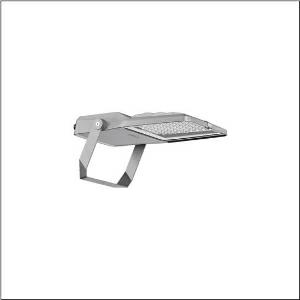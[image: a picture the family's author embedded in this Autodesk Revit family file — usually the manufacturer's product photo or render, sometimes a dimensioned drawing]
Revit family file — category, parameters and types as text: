
# Revit family: floodlight_fl_21_iq_mini___pl33t_5xa7771d4f1a_3e9c
name_source: partatom
category: Lighting Fixtures
units: mm (PartAtom-declared; Revit-internal decimal feet)

## family parameters
Cut with Voids When Loaded = No
Host = Face
Light Source = No
Part Type = Normal
Room Calculation Point = No
Round Connector Dimension = Use Diameter
Shared = No

## types (1)
- --- (1 x LED, 18390 lm, 143 W, 4000K)
    Apparent Load = 143 VA
    CIE Flux Codes = 26 75 99 100 100
    Color Rendering = 70
    Color Temperature = 4000K
    Default Elevation = 1800 mm
    Description = Floodlight FL 21 iQ mini, floodlight, primary light control with lens, of PMMA, primary optical cover: protective disc, of toughened safety glass, transparent, light distribution: PL33T, light emission: direct distribution, installation type: surface-mounted, lamps: LED, High Power LED, rated values: 18.390lm | 143W | 128,6lm/W (begin service life); end service life: 18.390lm | 151,6W; at 50% lumin. flux: 9.195lm | 60,8W | 151,2lm/W, colour temperature: 4000K, colour rendering: CRI > 70, light colour: 740, light setting 1 begin service life: 100% | 18.390lm | 143W | 128,6lm/W | 4.000K, light setting 1 end service life: 151,6W, further light settings possible, control: Auto-Match, Temp-Guard, Lumen-Switch, Night-Set, Smart-Wire, Light-Fading, Desk-Remote (wireless, voltage-free reading and setting of iQ features in the workshop via application-optimized NFC function/RFID function), optimised constant luminous flux control (CLO 2.0), pre-setting: linear dimming characteristic, with terminal, 6-pole, mains connection: 220..240V, AC, 50/60Hz, luminaire housing, of diecast aluminium, powder-coated, SITECO metallic grey (DB 702S), corrosivity category C5 mid according to DIN EN ISO 12944suitable for swimming poolschlorine-resistant, sealing non-destructively replaceable, mounting bracket, of steel, galvanised, powder-coated, SITECO metallic grey (DB 702S), protection rating (complete): IP66, insulation class (complete): insulation class II (safety insulation), certification: CE, ENEC, VDE, protection symbol: D, impact resistance: IK08, permissible operating ambient temperature: -40..+40°C, permissible operating ambient temperature for outdoor applications: -40..+50°C, standard: DIN EN 12944, LABS conformity tested according to VDMA 24364:2018-05, packaging unit: 1 piece

Light Distribution: PL33T
    Height = 70 mm
    Lamp = 1 x LED
    Lamp Light Flux = 18390 lm
    Lamp Power = 143 W
    Lamp count = 1
    Length = 485 mm
    Luminous efficacy = 129 lm/W
    Manufacturer = Siteco
    ModVariant = No
    Model = 5XA7771D4F1A
    Number of Poles = 1
    OnlyDefault = Yes
    Power Factor = 1
    Product Name = Floodlight FL 21 iQ mini | PL33T
    Product group = floodlight | pylon annexe
    ProductGroupID = 6201
    Protection Class = Protection class II
    Protection Degree = IP 66
    RLX_Detail_Level = 1
    RLX_Emergency_Light_Flux = 0 lm
    RLX_Emergency_Type = 0
    RLX_Emergency_Type_DB = No
    RlxData = <blob elided: 96697 chars, md5=aa1e23f1>
    Socket = socket
    Standby Power = 0 W
    System Light Flux = 18390 lm
    System Power = 143 W
    Type Comments = factory setting: luminous flux: 100 % | dim-lin: 254 | 730 mA
    Type Image = l_1006845.jpg
    URL = http://relux.com
    VarID = @adj_148655
    Voltage = 0 V
    Weight = 0.00 kg
    Width = 337 mm

## geometry (parser evidence)
native form markers: Blend x4, Sweep x10
no freeform markers — native parametric forms only
